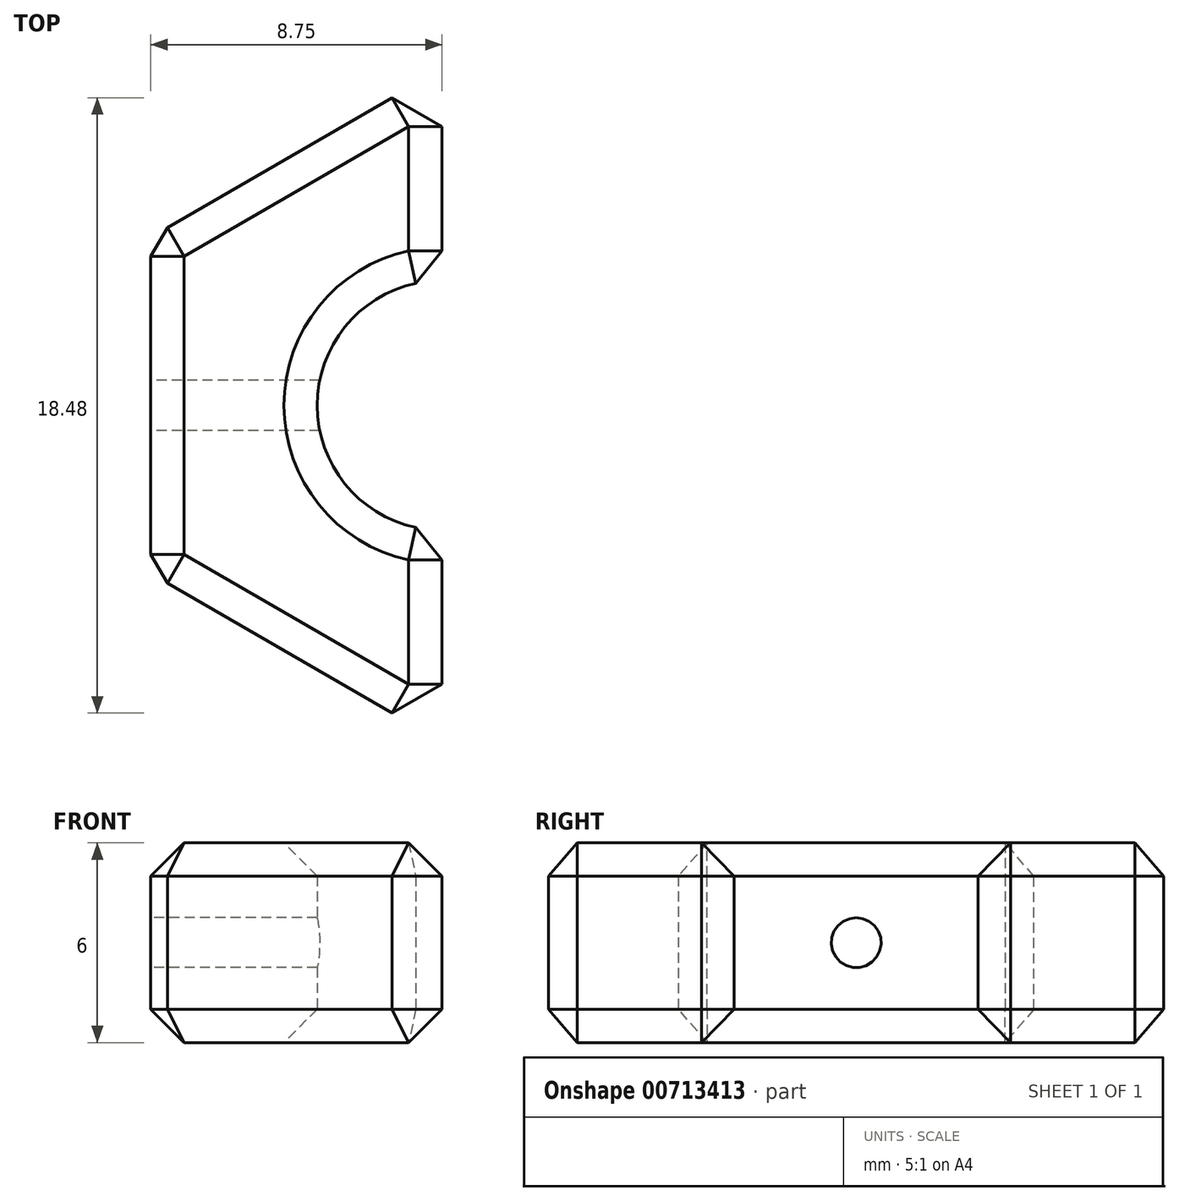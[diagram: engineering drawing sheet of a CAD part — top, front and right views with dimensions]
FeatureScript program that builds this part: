
annotation { "Feature Type Name" : "Feature", "Feature Type Description" : "" }
export const myFeature = defineFeature(function(context is Context, id is Id, definition is map)
    precondition{}
    {
        {
            var Q0;
            Q0=qCreatedBy(makeId("Top.planeOp"),FACE);
            var sketch = newSketch(context, id + "F0", { "sketchPlane" : qUnion([Q0])});
            skCircle(sketch, "E0.cCircle", {"center": v(0, 0) * mm, "radius": 8.75 * mm, "construction": true});
            skLineSegment(sketch, "E0.0", {"start": v(-8.75, -5.05) * mm, "end": v(-8.75, 5.05) * mm});
            skLineSegment(sketch, "E0.1", {"start": v(-8.75, 5.05) * mm, "end": v(0, 10.1) * mm});
            skLineSegment(sketch, "E0.2", {"start": v(0, 10.1) * mm, "end": v(8.75, 5.05) * mm});
            skLineSegment(sketch, "E0.3", {"start": v(8.75, 5.05) * mm, "end": v(8.75, -5.05) * mm});
            skLineSegment(sketch, "E0.4", {"start": v(8.75, -5.05) * mm, "end": v(0, -10.1) * mm});
            skLineSegment(sketch, "E0.5", {"start": v(0, -10.1) * mm, "end": v(-8.75, -5.05) * mm});
            skPoint(sketch, "E0.0.midPoint", {"position": v(-8.75, 0) * mm});
            skCircle(sketch, "E1", {"center": v(0, 0) * mm, "radius": 3.75 * mm});
            skLineSegment(sketch, "E2", {"start": v(0, 10.1) * mm, "end": v(0, -10.1) * mm});
            skSolve(sketch);
        }
        {
            var Q0;
            Q0=makeQuery(id+"F0.imprint","IMPRINT",FACE,{"disambiguationData":[TD([[makeQuery(id+"F0.imprint","IMPRINT",EDGE,{"derivedFrom":sQuery(id+"F0.wireOp",EDGE,"E0.0")}),-1.0]])]});
            extrude(context, id + "F1", {"entities" : qUnion([Q0]), "depth" : 6 * mm, "offsetDistance" : 25 * mm});
        }
        {
            var Q0;
            Q0=makeQuery(id+"F1.opExtrude","CAP_FACE",FACE,{"disambiguationData":[OSD([sQuery(id+"F0.wireOp",EDGE,"E0.0"),sQuery(id+"F0.wireOp",EDGE,"E0.1"),sQuery(id+"F0.wireOp",EDGE,"E0.5"),sQuery(id+"F0.wireOp",EDGE,"E1"),sQuery(id+"F0.wireOp",EDGE,"E2")])],"isStart":false});
            var Q1;
            Q1=makeQuery(id+"F1.opExtrude","CAP_FACE",FACE,{"disambiguationData":[OSD([sQuery(id+"F0.wireOp",EDGE,"E0.0"),sQuery(id+"F0.wireOp",EDGE,"E0.1"),sQuery(id+"F0.wireOp",EDGE,"E0.5"),sQuery(id+"F0.wireOp",EDGE,"E1"),sQuery(id+"F0.wireOp",EDGE,"E2")])],"isStart":true});
            var Q2;
            Q2=makeQuery(id+"F1.opExtrude","SWEPT_EDGE",EDGE,{"disambiguationData":[OSD([sQuery(id+"F0.wireOp",EDGE,"E0.4"),sQuery(id+"F0.wireOp",EDGE,"E0.5"),sQuery(id+"F0.wireOp",EDGE,"E2")])]});
            var Q3;
            {var subQ0=sQuery(id+"F0.wireOp",EDGE,"E2");var subQ1=sQuery(id+"F0.wireOp",EDGE,"E1");Q3=makeQuery(id+"F1.opExtrude","SWEPT_EDGE",EDGE,{"disambiguationData":[OSD([subQ1,subQ0]),TDD([makeQuery(id+"F0.imprint","INTERSECT",VERTEX,{"disambiguationData":[OD(1.0)],"derivedFrom":[subQ1,subQ0]})])]});}
            var Q4;
            {var subQ0=sQuery(id+"F0.wireOp",EDGE,"E2");var subQ1=sQuery(id+"F0.wireOp",EDGE,"E1");Q4=makeQuery(id+"F1.opExtrude","SWEPT_EDGE",EDGE,{"disambiguationData":[OSD([subQ1,subQ0]),TDD([makeQuery(id+"F0.imprint","INTERSECT",VERTEX,{"disambiguationData":[OD(0.0)],"derivedFrom":[subQ1,subQ0]})])]});}
            var Q5;
            Q5=makeQuery(id+"F1.opExtrude","SWEPT_EDGE",EDGE,{"disambiguationData":[OSD([sQuery(id+"F0.wireOp",EDGE,"E0.1"),sQuery(id+"F0.wireOp",EDGE,"E0.2"),sQuery(id+"F0.wireOp",EDGE,"E2")])]});
            var Q6;
            Q6=makeQuery(id+"F1.opExtrude","SWEPT_EDGE",EDGE,{"disambiguationData":[OSD([sQuery(id+"F0.wireOp",EDGE,"E0.0"),sQuery(id+"F0.wireOp",EDGE,"E0.5")])]});
            var Q7;
            Q7=makeQuery(id+"F1.opExtrude","SWEPT_EDGE",EDGE,{"disambiguationData":[OSD([sQuery(id+"F0.wireOp",EDGE,"E0.0"),sQuery(id+"F0.wireOp",EDGE,"E0.1")])]});
            chamfer(context, id + "F2", {"entities" : qUnion([Q0, Q1, Q2, Q3, Q4, Q5, Q6, Q7]), "width" : 1 * mm, "tangentPropagation" : true});
        }
        {
            var Q0;
            Q0=makeQuery(id+"F1.opExtrude","SWEPT_FACE",FACE,{"disambiguationData":[OSD([sQuery(id+"F0.wireOp",EDGE,"E0.0")])]});
            var sketch = newSketch(context, id + "F3", { "sketchPlane" : qUnion([Q0])});
            skCircle(sketch, "E3", {"center": v(0, 3) * mm, "radius": 0.75 * mm});
            skLineSegment(sketch, "E4", {"start": v(0, 3) * mm, "end": v(0, 5) * mm, "construction": true});
            skLineSegment(sketch, "E5", {"start": v(0, 3) * mm, "end": v(0, 1) * mm, "construction": true});
            skSolve(sketch);
        }
        {
            var Q0;
            Q0=makeQuery(id+"F3.imprint","IMPRINT",FACE,{"disambiguationData":[TD([[makeQuery(id+"F3.imprint","IMPRINT",EDGE,{"derivedFrom":sQuery(id+"F3.wireOp",EDGE,"E3")}),1.0]])]});
            extrude(context, id + "F4", {"entities" : qUnion([Q0]), "operationType" : NewBodyOperationType.REMOVE, "endBound" : BoundingType.THROUGH_ALL, "oppositeDirection" : true, "depth" : 25 * mm, "offsetDistance" : 25 * mm});
        }
    });
